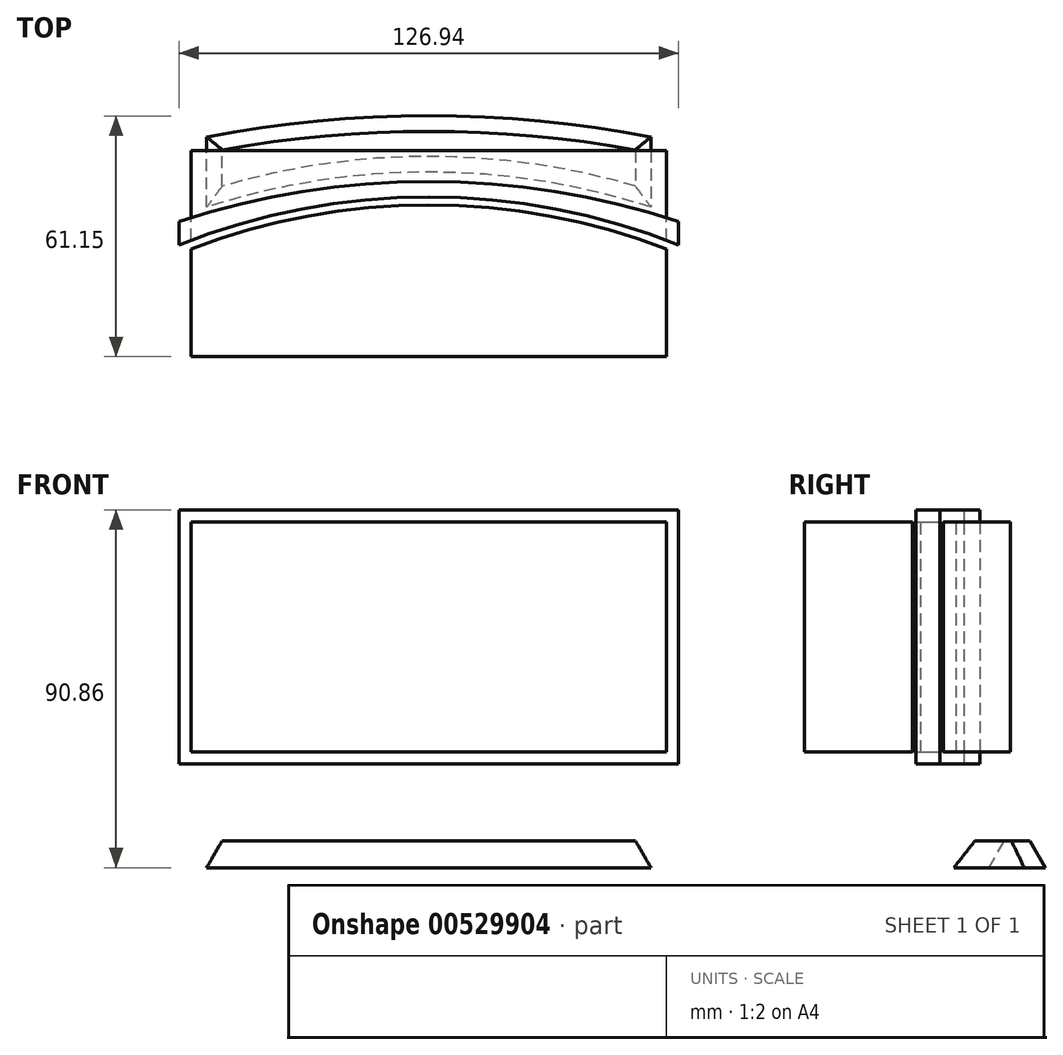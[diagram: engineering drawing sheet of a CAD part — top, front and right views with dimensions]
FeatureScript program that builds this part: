
annotation { "Feature Type Name" : "Feature", "Feature Type Description" : "" }
export const myFeature = defineFeature(function(context is Context, id is Id, definition is map)
    precondition{}
    {
        {
            var Q0;
            Q0=qCreatedBy(makeId("Top.planeOp"),FACE);
            var sketch = newSketch(context, id + "F0", { "sketchPlane" : qUnion([Q0])});
            skLineSegment(sketch, "E0.left", {"start": v(63.47, 0) * mm, "end": v(63.47, 8.2) * mm});
            skLineSegment(sketch, "E0.right", {"start": v(-63.47, 0) * mm, "end": v(-63.47, 8.2) * mm});
            skPoint(sketch, "E0.middle", {"position": v(0, 0) * mm});
            skArc(sketch, "E1", {"start": v(63.47, 8.2) * mm, "mid": v(0, 18.33) * mm, "end": v(-63.47, 8.2) * mm});
            skArc(sketch, "E2", {"start": v(63.47, 0) * mm, "mid": v(0, 12.37) * mm, "end": v(-63.47, 0) * mm});
            skPoint(sketch, "E3.orphan", {"position": v(-63.47, -8.2) * mm});
            skPoint(sketch, "E4.orphan", {"position": v(63.47, -8.2) * mm});
            skSolve(sketch);
        }
        {
            var Q0;
            Q0=makeQuery(id+"F0.imprint","IMPRINT",FACE,{"disambiguationData":[TD([[makeQuery(id+"F0.imprint","IMPRINT",EDGE,{"derivedFrom":sQuery(id+"F0.wireOp",EDGE,"E0.left")}),1.0]])]});
            extrude(context, id + "F1", {"entities" : qUnion([Q0]), "depth" : 64.52 * mm, "offsetDistance" : 25.4 * mm});
        }
        {
            var Q0;
            Q0=qCreatedBy(makeId("Front.planeOp"),FACE);
            var sketch = newSketch(context, id + "F2", { "sketchPlane" : qUnion([Q0])});
            skLineSegment(sketch, "E5.0", {"start": v(60.42, 61.47) * mm, "end": v(-60.42, 61.47) * mm});
            skLineSegment(sketch, "E5.1", {"start": v(60.42, 61.47) * mm, "end": v(60.42, 3.05) * mm});
            skLineSegment(sketch, "E5.2", {"start": v(60.42, 3.05) * mm, "end": v(-60.42, 3.05) * mm});
            skLineSegment(sketch, "E5.3", {"start": v(-60.42, 61.47) * mm, "end": v(-60.42, 3.05) * mm});
            skSolve(sketch);
        }
        {
            var Q0;
            Q0=makeQuery(id+"F2.imprint","IMPRINT",FACE,{"disambiguationData":[TD([[makeQuery(id+"F2.imprint","IMPRINT",EDGE,{"derivedFrom":sQuery(id+"F2.wireOp",EDGE,"E5.0")}),1.0]])]});
            extrude(context, id + "F3", {"entities" : qUnion([Q0]), "endBound" : BoundingType.SYMMETRIC, "depth" : 52.32 * mm, "offsetDistance" : 25.4 * mm});
        }
        {
            var Q0;
            Q0=makeQuery(id+"F3.opExtrude","SWEPT_BODY",BODY,{"disambiguationData":[OSD([sQuery(id+"F2.wireOp",EDGE,"E5.0"),sQuery(id+"F2.wireOp",EDGE,"E5.1"),sQuery(id+"F2.wireOp",EDGE,"E5.2"),sQuery(id+"F2.wireOp",EDGE,"E5.3")])]});
            var Q1;
            Q1=makeQuery(id+"F1.opExtrude","SWEPT_BODY",BODY,{"disambiguationData":[OSD([sQuery(id+"F0.wireOp",EDGE,"E0.left"),sQuery(id+"F0.wireOp",EDGE,"E0.right"),sQuery(id+"F0.wireOp",EDGE,"E1"),sQuery(id+"F0.wireOp",EDGE,"E2")])]});
            booleanBodies(context, id + "F4", {"operationType" : BooleanOperationType.INTERSECTION, "tools" : qUnion([Q0, Q1]), "keepTools" : true});
        }
        {
            var Q0;
            Q0=makeQuery(id+"F4.opBoolean","INTERSECT",BODY,{"derivedFrom":[makeQuery(id+"F1.opExtrude","SWEPT_BODY",BODY,{"disambiguationData":[OSD([sQuery(id+"F0.wireOp",EDGE,"E0.left"),sQuery(id+"F0.wireOp",EDGE,"E0.right"),sQuery(id+"F0.wireOp",EDGE,"E1"),sQuery(id+"F0.wireOp",EDGE,"E2")])]}),makeQuery(id+"F3.opExtrude","SWEPT_BODY",BODY,{"disambiguationData":[OSD([sQuery(id+"F2.wireOp",EDGE,"E5.0"),sQuery(id+"F2.wireOp",EDGE,"E5.1"),sQuery(id+"F2.wireOp",EDGE,"E5.2"),sQuery(id+"F2.wireOp",EDGE,"E5.3")])]})]});
            var Q1;
            Q1=makeQuery(id+"F1.opExtrude","SWEPT_BODY",BODY,{"disambiguationData":[OSD([sQuery(id+"F0.wireOp",EDGE,"E0.left"),sQuery(id+"F0.wireOp",EDGE,"E0.right"),sQuery(id+"F0.wireOp",EDGE,"E1"),sQuery(id+"F0.wireOp",EDGE,"E2")])]});
            booleanBodies(context, id + "F5", {"operationType" : BooleanOperationType.SUBTRACTION, "tools" : qUnion([Q0]), "targets" : qUnion([Q1]), "keepTools" : true});
        }
        {
            var Q0;
            Q0=makeQuery(id+"F1.opExtrude","CAP_FACE",FACE,{"disambiguationData":[OSD([sQuery(id+"F0.wireOp",EDGE,"E0.left"),sQuery(id+"F0.wireOp",EDGE,"E0.right"),sQuery(id+"F0.wireOp",EDGE,"E1"),sQuery(id+"F0.wireOp",EDGE,"E2")])],"isStart":false});
            var sketch = newSketch(context, id + "F6", { "sketchPlane" : qUnion([Q0])});
            skArc(sketch, "E6.0", {"start": v(64.23, 1.88) * mm, "mid": v(0, 14.4) * mm, "end": v(-64.23, 1.88) * mm});
            skSolve(sketch);
        }
        {
            var Q0;
            {var subQ5=makeQuery(id+"F1.opExtrude","CAP_EDGE",EDGE,{"disambiguationData":[OSD([sQuery(id+"F0.wireOp",EDGE,"E2")])],"isStart":false});Q0=makeQuery(id+"F6.imprint","IMPRINT",FACE,{"disambiguationData":[TD([[makeQuery(id+"F6.imprint","IMPRINT",EDGE,{"derivedFrom":subQ5}),-1.0]])]});}
            extrude(context, id + "F7", {"entities" : qUnion([Q0]), "operationType" : NewBodyOperationType.REMOVE, "oppositeDirection" : true, "depth" : 79.25 * mm, "offsetDistance" : 25.4 * mm});
        }
        {
            var Q0;
            Q0=qCreatedBy(makeId("Front.planeOp"),FACE);
            var sketch = newSketch(context, id + "F8", { "sketchPlane" : qUnion([Q0])});
            skLineSegment(sketch, "E7", {"start": v(-76.78, -26.34) * mm, "end": v(77.02, -26.34) * mm});
            skSolve(sketch);
        }
        {
            var Q0;
            Q0=sQuery(id+"F8.wireOp",EDGE,"E7");
            extrude(context, id + "F9", {"bodyType" : ToolBodyType.SURFACE, "surfaceEntities" : qUnion([Q0]), "endBound" : BoundingType.SYMMETRIC, "depth" : 116.33 * mm, "offsetDistance" : 25.4 * mm});
        }
        {
            var Q0;
            Q0=makeQuery(id+"F9.opExtrude","SWEPT_FACE",FACE,{"disambiguationData":[OSD([sQuery(id+"F8.wireOp",EDGE,"E7")])]});
            var sketch = newSketch(context, id + "F10", { "sketchPlane" : qUnion([Q0])});
            skLineSegment(sketch, "E8.left", {"start": v(56.44, -29.65) * mm, "end": v(56.44, -11.77) * mm});
            skLineSegment(sketch, "E8.right", {"start": v(-56.44, -29.65) * mm, "end": v(-56.44, -11.77) * mm});
            skPoint(sketch, "E8.middle", {"position": v(0, -20.71) * mm});
            skArc(sketch, "E9", {"start": v(-56.44, -11.77) * mm, "mid": v(0, -20.71) * mm, "end": v(56.44, -11.77) * mm});
            skArc(sketch, "E10", {"start": v(-56.44, -29.65) * mm, "mid": v(0, -35) * mm, "end": v(56.44, -29.65) * mm});
            skSolve(sketch);
        }
        {
            var Q0;
            Q0=makeQuery(id+"F10.imprint","IMPRINT",FACE,{"disambiguationData":[TD([[makeQuery(id+"F10.imprint","IMPRINT",EDGE,{"derivedFrom":sQuery(id+"F10.wireOp",EDGE,"E8.left")}),1.0]])]});
            extrude(context, id + "F11", {"entities" : qUnion([Q0]), "oppositeDirection" : true, "depth" : 6.86 * mm, "offsetDistance" : 25.4 * mm, "hasDraft" : true, "draftAngle" : 30 * degree, "draftPullDirection" : true});
        }
    });
